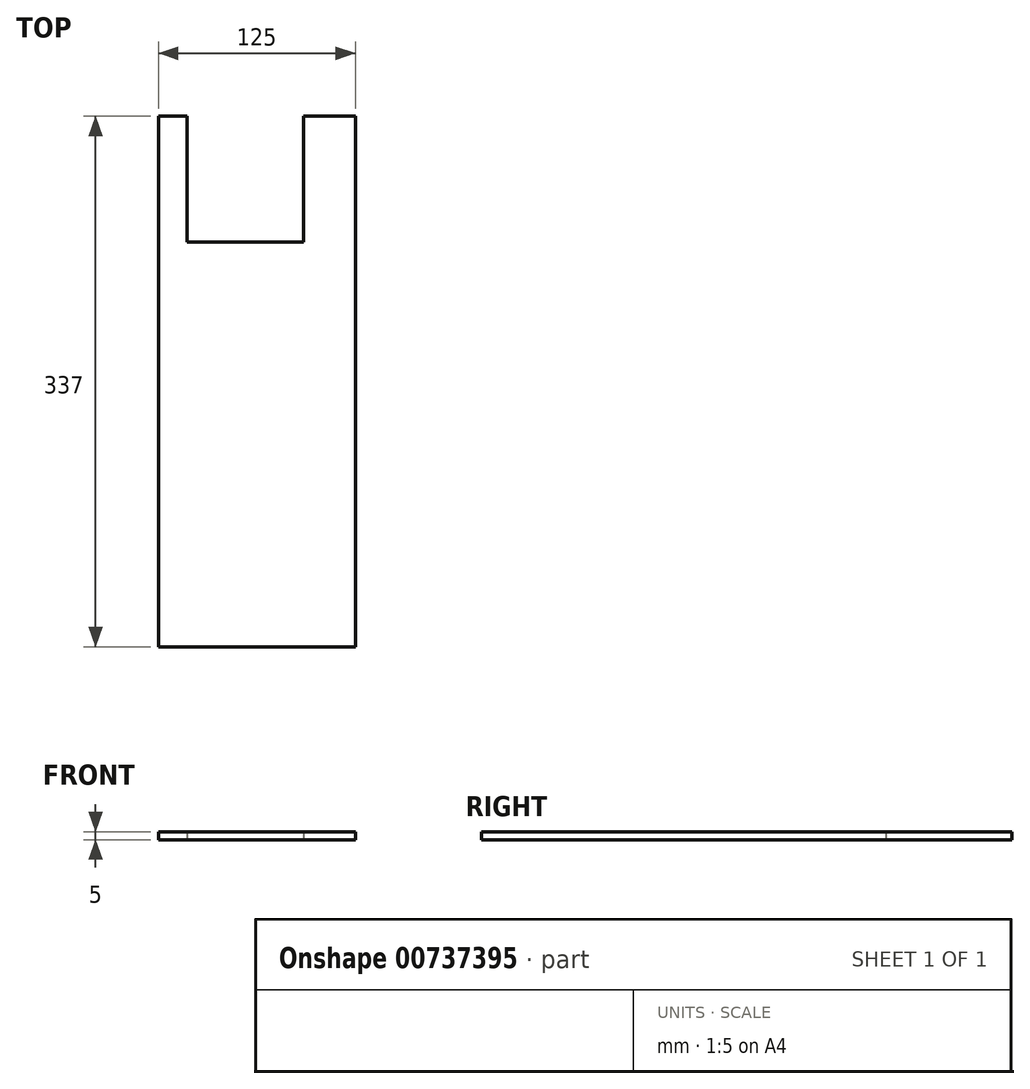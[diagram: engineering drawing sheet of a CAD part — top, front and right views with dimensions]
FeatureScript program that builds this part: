
annotation { "Feature Type Name" : "Feature", "Feature Type Description" : "" }
export const myFeature = defineFeature(function(context is Context, id is Id, definition is map)
    precondition{}
    {
        {
            var Q0;
            Q0=qCreatedBy(makeId("Top.planeOp"),FACE);
            var sketch = newSketch(context, id + "F0", { "sketchPlane" : qUnion([Q0])});
            skLineSegment(sketch, "E0.bottom", {"start": v(62.5, 168.5) * mm, "end": v(29.5, 168.5) * mm});
            skLineSegment(sketch, "E0.top", {"start": v(62.5, -168.5) * mm, "end": v(-62.5, -168.5) * mm});
            skLineSegment(sketch, "E0.left", {"start": v(62.5, 168.5) * mm, "end": v(62.5, -168.5) * mm});
            skLineSegment(sketch, "E0.right", {"start": v(-62.5, 168.5) * mm, "end": v(-62.5, -168.5) * mm});
            skPoint(sketch, "E0.middle", {"position": v(0, 0) * mm});
            skLineSegment(sketch, "E1", {"start": v(-62.5, 168.5) * mm, "end": v(-44.5, 168.5) * mm});
            skLineSegment(sketch, "E2", {"start": v(-44.5, 168.5) * mm, "end": v(-44.5, 88.5) * mm});
            skLineSegment(sketch, "E3", {"start": v(-44.5, 88.5) * mm, "end": v(29.5, 88.5) * mm});
            skLineSegment(sketch, "E4", {"start": v(29.5, 168.5) * mm, "end": v(29.5, 88.5) * mm});
            skLineSegment(sketch, "E5.trimOffspring", {"start": v(-44.5, 168.5) * mm, "end": v(-62.5, 168.5) * mm});
            skSolve(sketch);
        }
        {
            var Q0;
            Q0=makeQuery(id+"F0.imprint","IMPRINT",FACE,{"disambiguationData":[TD([[makeQuery(id+"F0.imprint","IMPRINT",EDGE,{"derivedFrom":sQuery(id+"F0.wireOp",EDGE,"E0.bottom")}),1.0]])]});
            extrude(context, id + "F1", {"entities" : qUnion([Q0]), "depth" : 5 * mm, "offsetDistance" : 25 * mm});
        }
    });
